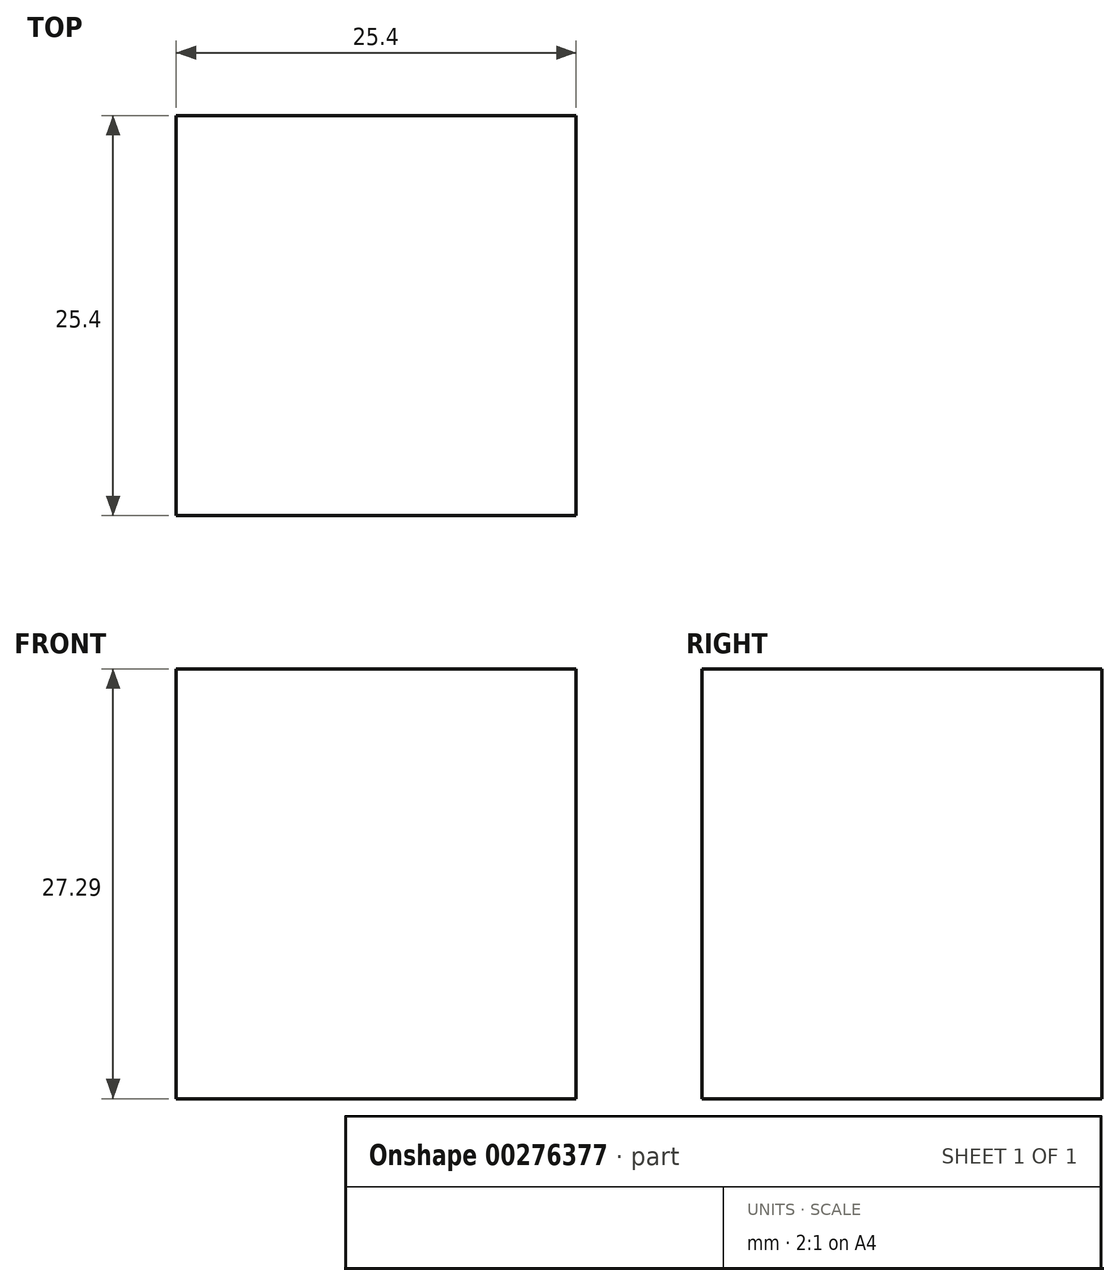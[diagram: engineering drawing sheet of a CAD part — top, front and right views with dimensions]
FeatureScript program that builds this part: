
annotation { "Feature Type Name" : "Feature", "Feature Type Description" : "" }
export const myFeature = defineFeature(function(context is Context, id is Id, definition is map)
    precondition{}
    {
        {
            var Q0;
            Q0=qCreatedBy(makeId("Front.planeOp"),FACE);
            var sketch = newSketch(context, id + "F0", { "sketchPlane" : qUnion([Q0])});
            skLineSegment(sketch, "E0.bottom", {"start": v(-43.58, 41.7) * mm, "end": v(-18.18, 41.7) * mm});
            skLineSegment(sketch, "E0.top", {"start": v(-43.58, 14.4) * mm, "end": v(-18.18, 14.4) * mm});
            skLineSegment(sketch, "E0.left", {"start": v(-43.58, 41.7) * mm, "end": v(-43.58, 14.4) * mm});
            skLineSegment(sketch, "E0.right", {"start": v(-18.18, 41.7) * mm, "end": v(-18.18, 14.4) * mm});
            skSolve(sketch);
        }
        {
            var Q0;
            Q0=makeQuery(id+"F0.imprint","IMPRINT",FACE,{"disambiguationData":[TD([[makeQuery(id+"F0.imprint","IMPRINT",EDGE,{"derivedFrom":sQuery(id+"F0.wireOp",EDGE,"E0.bottom")}),-1.0]])]});
            extrude(context, id + "F1", {"entities" : qUnion([Q0]), "depth" : 25.4 * mm});
        }
    });
